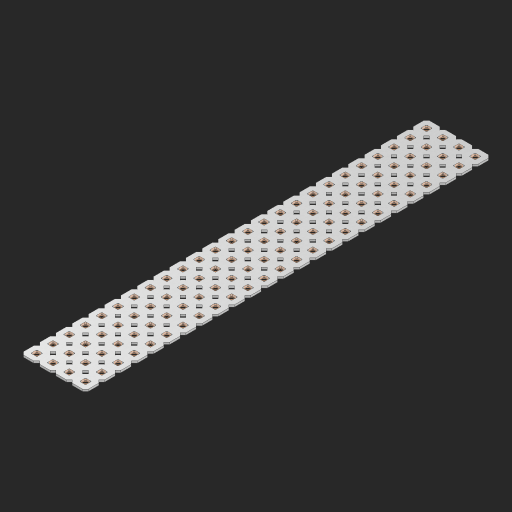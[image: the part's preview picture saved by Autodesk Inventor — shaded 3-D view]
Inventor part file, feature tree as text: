
AUTODESK INVENTOR PART (.ipt)
format: ipt  version: 2023 (Build 270158000, 158)  size: 1,435,648 bytes
history: native  units: in
note: dims shown in document units (in); Inventor stores cm internally (conversion verified against a paired STEP export)
features: other x101, extrude x99, sketch x2, pattern_linear x1
ambient origin geometry x8: Origin, YZ Plane, XZ Plane, XY Plane, X Axis, Y Axis, Z Axis, Center Point
bodies: Solid1 (feature_tree), Body (feature_tree)
feature tree (203):
  pattern_linear  "Rectangular Pattern1"  Spacing1=0.09in  [1 undecoded]
  sketch  "Sketch1"  dims[d1=0.5in]
  sketch  "Sketch2"  dims[d2=0.182in d3=0.09in d4=0.09in d5=0.09in d6=0.09in d7=0.09in d8=0.09in d9=0.09in d10=0.09in d11=0.02in d13=0.0in d14=0.172in d15=0.0625in d16=0.0in d19=0.5in d22=0.5in]
  other  "Srf1"
  other  "Srf126"
  other  "Srf127"
  other  "Srf128"
  other  "Srf129"
  other  "Srf130"
  other  "Srf131"
  other  "Srf250"
  other  "Srf251"
  other  "Srf252"
  other  "Srf253"
  other  "Srf254"
  other  "Srf255"
  other  "Srf256"
  other  "Srf257"
  other  "Srf258"
  other  "Srf259"
  other  "Srf260"
  other  "Srf261"
  other  "Srf262"
  other  "Srf263"
  other  "Srf264"
  other  "Srf265"
  other  "Srf266"
  other  "Srf267"
  other  "Srf268"
  other  "Srf269"
  other  "Srf270"
  other  "Srf271"
  other  "Srf272"
  other  "Srf273"
  other  "Srf274"
  other  "Srf275"
  other  "Srf276"
  other  "Srf277"
  other  "Srf278"
  other  "Srf279"
  other  "Srf280"
  other  "Srf281"
  other  "Srf282"
  other  "Srf283"
  other  "Srf284"
  other  "Srf285"
  other  "Srf286"
  other  "Srf287"
  other  "Srf288"
  other  "Srf289"
  other  "Srf290"
  other  "Srf291"
  other  "Srf292"
  other  "Srf293"
  other  "Srf294"
  other  "Srf295"
  other  "Srf296"
  other  "Srf297"
  other  "Srf298"
  other  "Srf299"
  other  "Srf300"
  other  "Srf301"
  other  "Srf302"
  other  "Srf303"
  other  "Srf304"
  other  "Srf305"
  other  "Srf306"
  other  "Srf307"
  other  "Srf308"
  other  "Srf309"
  other  "Srf310"
  other  "Srf311"
  other  "Srf312"
  other  "Srf313"
  other  "Srf314"
  other  "Srf315"
  other  "Srf316"
  other  "Srf317"
  other  "Srf318"
  other  "Srf319"
  other  "Srf320"
  other  "Srf321"
  other  "Srf322"
  other  "Srf323"
  other  "Srf324"
  other  "Srf325"
  other  "Srf326"
  other  "Srf327"
  other  "Srf328"
  other  "Srf329"
  other  "Srf330"
  other  "Srf331"
  other  "Srf332"
  other  "Srf333"
  other  "Srf334"
  other  "Srf335"
  other  "Srf336"
  other  "Srf337"
  other  "Srf338"
  other  "Srf339"
  other  "Srf340"
  other  "Srf341"
  other  "Srf342"
  other  "Circle"
  extrude  "ExtrusionSrf126"  Depth=0.09in
  extrude  "ExtrusionSrf127"  Depth=0.09in
  extrude  "ExtrusionSrf128"  Depth=0.09in
  extrude  "ExtrusionSrf129"  Depth=0.09in
  extrude  "ExtrusionSrf130"  Depth=0.09in
  extrude  "ExtrusionSrf131"  Depth=0.09in
  extrude  "ExtrusionSrf250"  Depth=0.09in
  extrude  "ExtrusionSrf251"  Depth=0.02in
  extrude  "ExtrusionSrf252"  TaperAngle=0.0deg  [1 undecoded]
  extrude  "ExtrusionSrf253"  Depth=0.5in
  extrude  "ExtrusionSrf254"  Depth=0.0625in TaperAngle=0.0deg
  extrude  "ExtrusionSrf255"  Depth=0.5in
  extrude  "ExtrusionSrf256"  Depth=0.5in
  extrude  "ExtrusionSrf257"  [1 undecoded]
  extrude  "ExtrusionSrf258"  [1 undecoded]
  extrude  "ExtrusionSrf259"  [1 undecoded]
  extrude  "ExtrusionSrf260"  [1 undecoded]
  extrude  "ExtrusionSrf261"  [1 undecoded]
  extrude  "ExtrusionSrf262"  [1 undecoded]
  extrude  "ExtrusionSrf263"  [1 undecoded]
  extrude  "ExtrusionSrf264"  [1 undecoded]
  extrude  "ExtrusionSrf265"  [1 undecoded]
  extrude  "ExtrusionSrf266"  [1 undecoded]
  extrude  "ExtrusionSrf267"  [1 undecoded]
  extrude  "ExtrusionSrf268"  [1 undecoded]
  extrude  "ExtrusionSrf269"  [1 undecoded]
  extrude  "ExtrusionSrf270"  [1 undecoded]
  extrude  "ExtrusionSrf271"  [1 undecoded]
  extrude  "ExtrusionSrf272"  [1 undecoded]
  extrude  "ExtrusionSrf273"  [1 undecoded]
  extrude  "ExtrusionSrf274"  [1 undecoded]
  extrude  "ExtrusionSrf275"  [1 undecoded]
  extrude  "ExtrusionSrf276"  [1 undecoded]
  extrude  "ExtrusionSrf277"  [1 undecoded]
  extrude  "ExtrusionSrf278"  [1 undecoded]
  extrude  "ExtrusionSrf279"  [1 undecoded]
  extrude  "ExtrusionSrf280"  [1 undecoded]
  extrude  "ExtrusionSrf281"  [1 undecoded]
  extrude  "ExtrusionSrf282"  [1 undecoded]
  extrude  "ExtrusionSrf283"  [1 undecoded]
  extrude  "ExtrusionSrf284"  [1 undecoded]
  extrude  "ExtrusionSrf285"  [1 undecoded]
  extrude  "ExtrusionSrf286"  [1 undecoded]
  extrude  "ExtrusionSrf287"  [1 undecoded]
  extrude  "ExtrusionSrf288"  [1 undecoded]
  extrude  "ExtrusionSrf289"  [1 undecoded]
  extrude  "ExtrusionSrf290"  [1 undecoded]
  extrude  "ExtrusionSrf291"  [1 undecoded]
  extrude  "ExtrusionSrf292"  [1 undecoded]
  extrude  "ExtrusionSrf293"  [1 undecoded]
  extrude  "ExtrusionSrf294"  [1 undecoded]
  extrude  "ExtrusionSrf295"  [1 undecoded]
  extrude  "ExtrusionSrf296"  [1 undecoded]
  extrude  "ExtrusionSrf297"  [1 undecoded]
  extrude  "ExtrusionSrf298"  [1 undecoded]
  extrude  "ExtrusionSrf299"  [1 undecoded]
  extrude  "ExtrusionSrf300"  [1 undecoded]
  extrude  "ExtrusionSrf301"  [1 undecoded]
  extrude  "ExtrusionSrf302"  [1 undecoded]
  extrude  "ExtrusionSrf303"  [1 undecoded]
  extrude  "ExtrusionSrf304"  [1 undecoded]
  extrude  "ExtrusionSrf305"  [1 undecoded]
  extrude  "ExtrusionSrf306"  [1 undecoded]
  extrude  "ExtrusionSrf307"  [1 undecoded]
  extrude  "ExtrusionSrf308"  [1 undecoded]
  extrude  "ExtrusionSrf309"  [1 undecoded]
  extrude  "ExtrusionSrf310"  [1 undecoded]
  extrude  "ExtrusionSrf311"  [1 undecoded]
  extrude  "ExtrusionSrf312"  [1 undecoded]
  extrude  "ExtrusionSrf313"  [1 undecoded]
  extrude  "ExtrusionSrf314"  [1 undecoded]
  extrude  "ExtrusionSrf315"  [1 undecoded]
  extrude  "ExtrusionSrf316"  [1 undecoded]
  extrude  "ExtrusionSrf317"  [1 undecoded]
  extrude  "ExtrusionSrf318"  [1 undecoded]
  extrude  "ExtrusionSrf319"  [1 undecoded]
  extrude  "ExtrusionSrf320"  [1 undecoded]
  extrude  "ExtrusionSrf321"  [1 undecoded]
  extrude  "ExtrusionSrf322"  [1 undecoded]
  extrude  "ExtrusionSrf323"  [1 undecoded]
  extrude  "ExtrusionSrf324"  [1 undecoded]
  extrude  "ExtrusionSrf325"  [1 undecoded]
  extrude  "ExtrusionSrf326"  [1 undecoded]
  extrude  "ExtrusionSrf327"  [1 undecoded]
  extrude  "ExtrusionSrf328"  [1 undecoded]
  extrude  "ExtrusionSrf329"  [1 undecoded]
  extrude  "ExtrusionSrf330"  [1 undecoded]
  extrude  "ExtrusionSrf331"  [1 undecoded]
  extrude  "ExtrusionSrf332"  [1 undecoded]
  extrude  "ExtrusionSrf333"  [1 undecoded]
  extrude  "ExtrusionSrf334"  [1 undecoded]
  extrude  "ExtrusionSrf335"  [1 undecoded]
  extrude  "ExtrusionSrf336"  [1 undecoded]
  extrude  "ExtrusionSrf337"  [1 undecoded]
  extrude  "ExtrusionSrf338"  [1 undecoded]
  extrude  "ExtrusionSrf339"  [1 undecoded]
  extrude  "ExtrusionSrf340"  [1 undecoded]
  extrude  "ExtrusionSrf341"  [1 undecoded]
  extrude  "ExtrusionSrf342"  [1 undecoded]
note: 88 required parameter values undecoded (feature->parameter linkage not recoverable at this tier; creation-order binding heuristic only, values carry confidence <= 0.55)
